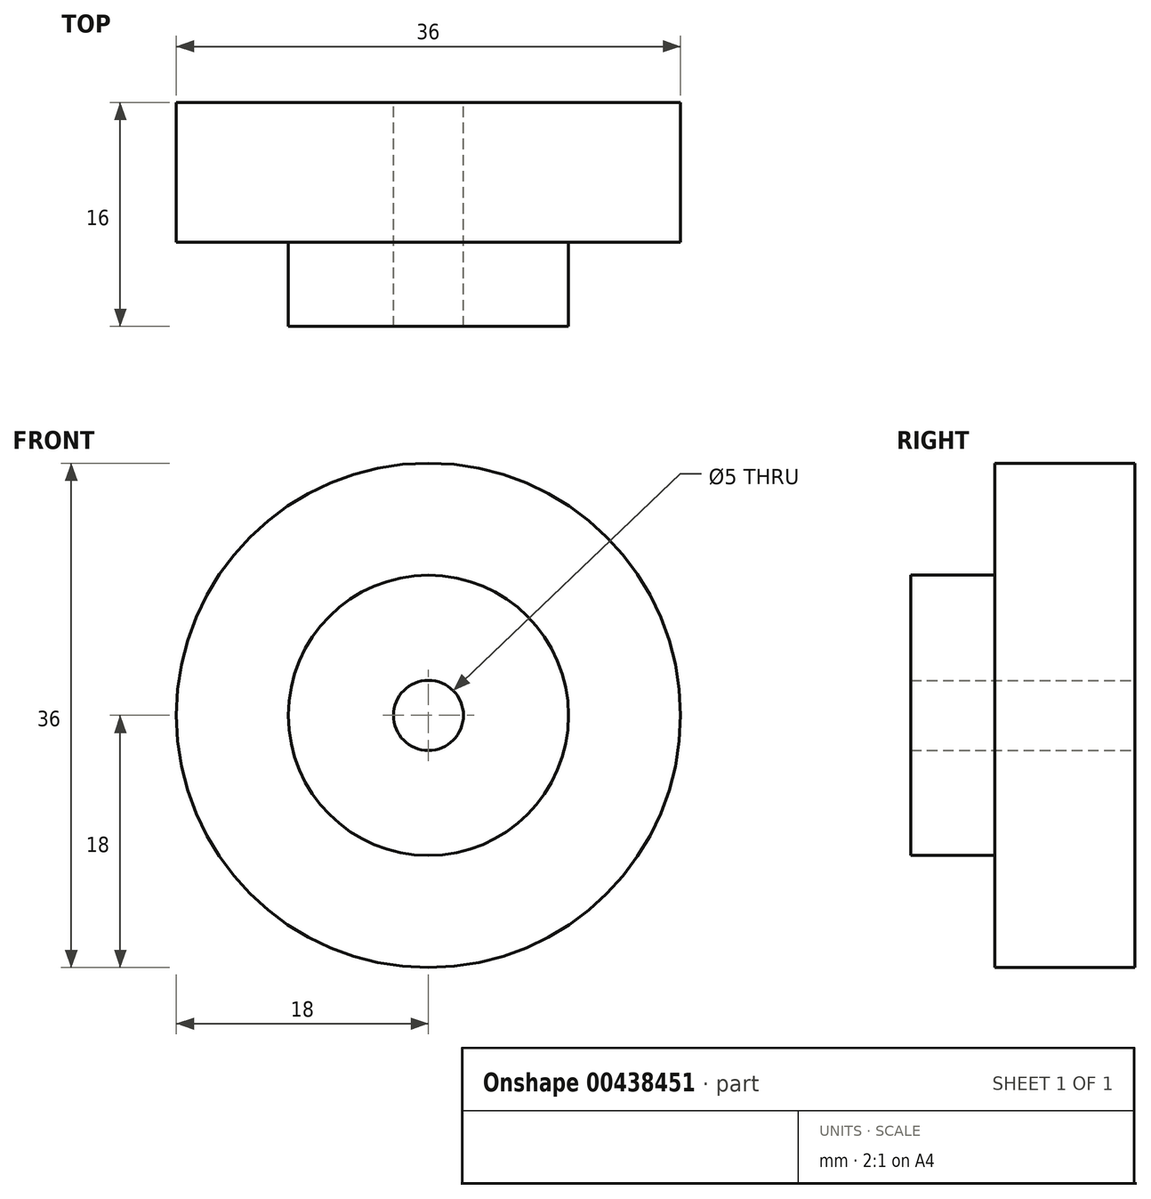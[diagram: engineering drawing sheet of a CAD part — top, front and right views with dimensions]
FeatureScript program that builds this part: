
annotation { "Feature Type Name" : "Feature", "Feature Type Description" : "" }
export const myFeature = defineFeature(function(context is Context, id is Id, definition is map)
    precondition{}
    {
        {
            var Q0;
            Q0=qCreatedBy(makeId("Front.planeOp"),FACE);
            var sketch = newSketch(context, id + "F0", { "sketchPlane" : qUnion([Q0])});
            skCircle(sketch, "E0", {"center": v(0, 0) * mm, "radius": 18 * mm});
            skCircle(sketch, "E1", {"center": v(0, 0) * mm, "radius": 10 * mm});
            skSolve(sketch);
        }
        {
            var Q0;
            Q0=makeQuery(id+"F0.imprint","IMPRINT",FACE,{"disambiguationData":[TD([[makeQuery(id+"F0.imprint","IMPRINT",EDGE,{"derivedFrom":sQuery(id+"F0.wireOp",EDGE,"E0")}),1.0]])]});
            extrude(context, id + "F1", {"entities" : qUnion([Q0]), "depth" : 10 * mm});
        }
        {
            var Q0;
            Q0=makeQuery(id+"F0.imprint","IMPRINT",FACE,{"disambiguationData":[TD([[makeQuery(id+"F0.imprint","IMPRINT",EDGE,{"derivedFrom":sQuery(id+"F0.wireOp",EDGE,"E1")}),1.0]])]});
            extrude(context, id + "F2", {"entities" : qUnion([Q0]), "operationType" : NewBodyOperationType.ADD, "depth" : 16 * mm});
        }
        {
            var Q0;
            Q0=sQuery(id+"F0.wireOp",VERTEX,"E0.center");
            var Q1;
            Q1=makeQuery(id+"F1.opExtrude","SWEPT_BODY",BODY,{"disambiguationData":[OSD([sQuery(id+"F0.wireOp",EDGE,"E0"),sQuery(id+"F0.wireOp",EDGE,"E1")])]});
            hole(context, id + "F3", {"style" : HoleStyle.SIMPLE, "endStyle" : HoleEndStyle.THROUGH, "oppositeDirection" : true, "holeDiameter" : 5 * mm, "isTappedThrough" : true, "tappedDepth" : 12 * mm, "tapClearance" : 3, "locations" : qUnion([Q0]), "scope" : qUnion([Q1])});
        }
    });
